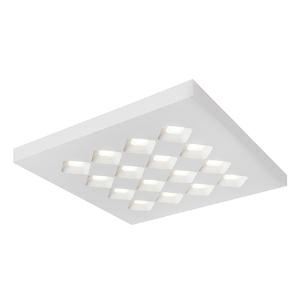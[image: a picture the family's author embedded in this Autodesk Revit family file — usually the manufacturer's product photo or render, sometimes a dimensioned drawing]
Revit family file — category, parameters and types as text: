
# Revit family: 3f_filippi_-_3f_diagon_p_soft_ugr_3f_filippi_-_12132_-_3f_diagon_p_25w-840_ep_soft_ugr_596x596
name_source: partatom
category: Lighting Fixtures
units: mm (PartAtom-declared; Revit-internal decimal feet)

## family parameters
Cut with Voids When Loaded = No
Host = Face
Light Source = No
Part Type = Normal
Room Calculation Point = No
Round Connector Dimension = Use Diameter
Shared = No

## types (1)
- 3F Filippi - 3F Dìagon P Soft UGR (1 x LED, 3679 lm, 29 W, 4000 K)
    Apparent Load = 29 VA
    Approval mark = ENEC
    CIE Flux Codes = 59 92 100 100 100
    Color Rendering = 80
    Color Temperature = 4000 K
    Control Gear = Electronic ballast
    Default Elevation = 1800 mm
    Description = ILLUMINOTECHNICAL
Luminous efficiency 100% (DLOR 100%, ULOR 0%).
Initial luminous flux of the luminaire 3679 lm.
Emergency luminaire luminous flux BLF 19.8%.
Direct symmetric distribution.
Installation Interdistance Transv.D = 1.23 x hu - Long.D = 1.23 x hu.
Average luminance <3000 cd/m² for radial angles >65°.
Tabular UGR (CIE 117 - 4H-8H; S=0.25H; 70/50/20): RUG 18.7 - 18.7.
Beam angle: 102° - 101°.
Luminous efficacy 127 lm/W.
Lifetime (L95/B10): 30000 h. (tq+25°C)
Lifetime (L90/B10): 50000 h. (tq+25°C)
Lifetime (L80/B10): 80000 h. (tq+25°C)
Lifetime (L75/B10): 100000 h. (tq+25°C)
Sudden decreased luminous flux after 50000 hours: 0% (C0).
Photobiological safety in compliance with IEC/TR 62778: RG0 risk exempt, (IEC 62471).
In compliance with IEC/EN 62722-2-1 - IEC/EN 62717 standards.

SOURCE
Squared LED module 25W/840.
Energy efficiency class (UE 2019/2020 - UE 2019/2015): C.
CIE 13.3 Colour rendering index: CRI >80 (R9 <50%).
IES TM-30 Fidelity Index: Rf = 84 Rg = 95.
CCT nominal colour temperature 4000 K.
Colour initial tolerance (MacAdam): SDCM 3.

MECHANICAL
White painted frame.
Height only 40 mm.
Housing in hot-galvanised steel, painted in white polyester.
Honeycombed diagonal screen in white anti-glare polycarbonate.
Opal methacrylate (PMMA) rhomboid lenses with differentiated, engraved and prismatic surfaces for diffused, soft lighting and excellent visual comfort.
Luminaire with limited surface temperature. - D - (EN 60598-2-24)
Dimensions: 596x596 mm, height 40 mm. Weight 6.5 kg.
IP40 protection degree.
Mechanical strength to impacts IK06 (1 joule).
Glow-wire test resistance 650°C.

ELECTRICAL
Halogen Free electronic wiring 230V-50/60Hz, power factor 0.90, THD <25%, constant output current, class I, 1 driver.
Power of the luminaire 29 W.
CE - IEC 60598-1 - EN 60598-1.
EP maintained emergency wiring on board, 1h duration, 24h recharge; compliant with EN 60598-2-22, excluding high risk areas.
SAFE FLICKER: PstLM=<1 and SVM=<0.4 (IEC TR 61547-1 and IEC TR 63158), to ensure a more comfortable and safe light.
Ambient temperature from +5°C to +25°C.
Temperature class T6 max 85°C.
Quick connection.
Relative humidity UR: <85%.

INSTALLATION
Ceiling.

APPLICATIONS
Environments: staterooms, with VDTs, offices.
Environments with exacting visual tasks, where diffused soft light for optimum visual comfort is required.

WARNING
Luminaire designed for disposal/recycling at end-of-life.
Replaceable (LED only) light source by a professional. Replaceable control gear by a professional.
    Height = 40 mm
    Lamp = 1 x LED
    Lamp Light Flux = 3679 lm
    Lamp Power = 29 W
    Lamp count = 1
    Length = 596 mm
    Lifetime = 50000 h
    Luminous efficacy = 127 lm/W
    Manufacturer = 3F Filippi
    ModVariant = No
    Model = 3F Filippi - 12132 - 3F Diagon P 25W-840 EP SOFT UGR 596x596
    Mounting Place = Ceiling
    Mounting Type = Surface mounted
    Number of Poles = 1
    OnlyDefault = Yes
    Power Factor = 1
    Product Name = 3F Filippi - 3F Dìagon P Soft UGR
    Product group = ceiling mounted luminaire
    ProductGroupID = 3
    Protection Class = Protection class I
    Protection Degree = IP 40
    RLX_Detail_Level = 1
    RLX_Emergency_Light_Flux = 0 lm
    RLX_Emergency_Type = 0
    RLX_Emergency_Type_DB = No
    RlxData = <blob elided: 94117 chars, md5=2048a1e0>
    Socket = socket
    Standby Power = 0 W
    System Light Flux = 3679 lm
    System Power = 29 W
    Type Comments = Product without accessories
    Type Image = 3ffilippi_3f_diagon_p_soft_ugr.jpg
    URL = http://relux.com
    VarID = ---
    Voltage = 0 V
    Weight = 0.00 kg
    Width = 596 mm

## geometry (parser evidence)
native form markers: Blend x4, Sweep x9
no freeform markers — native parametric forms only
